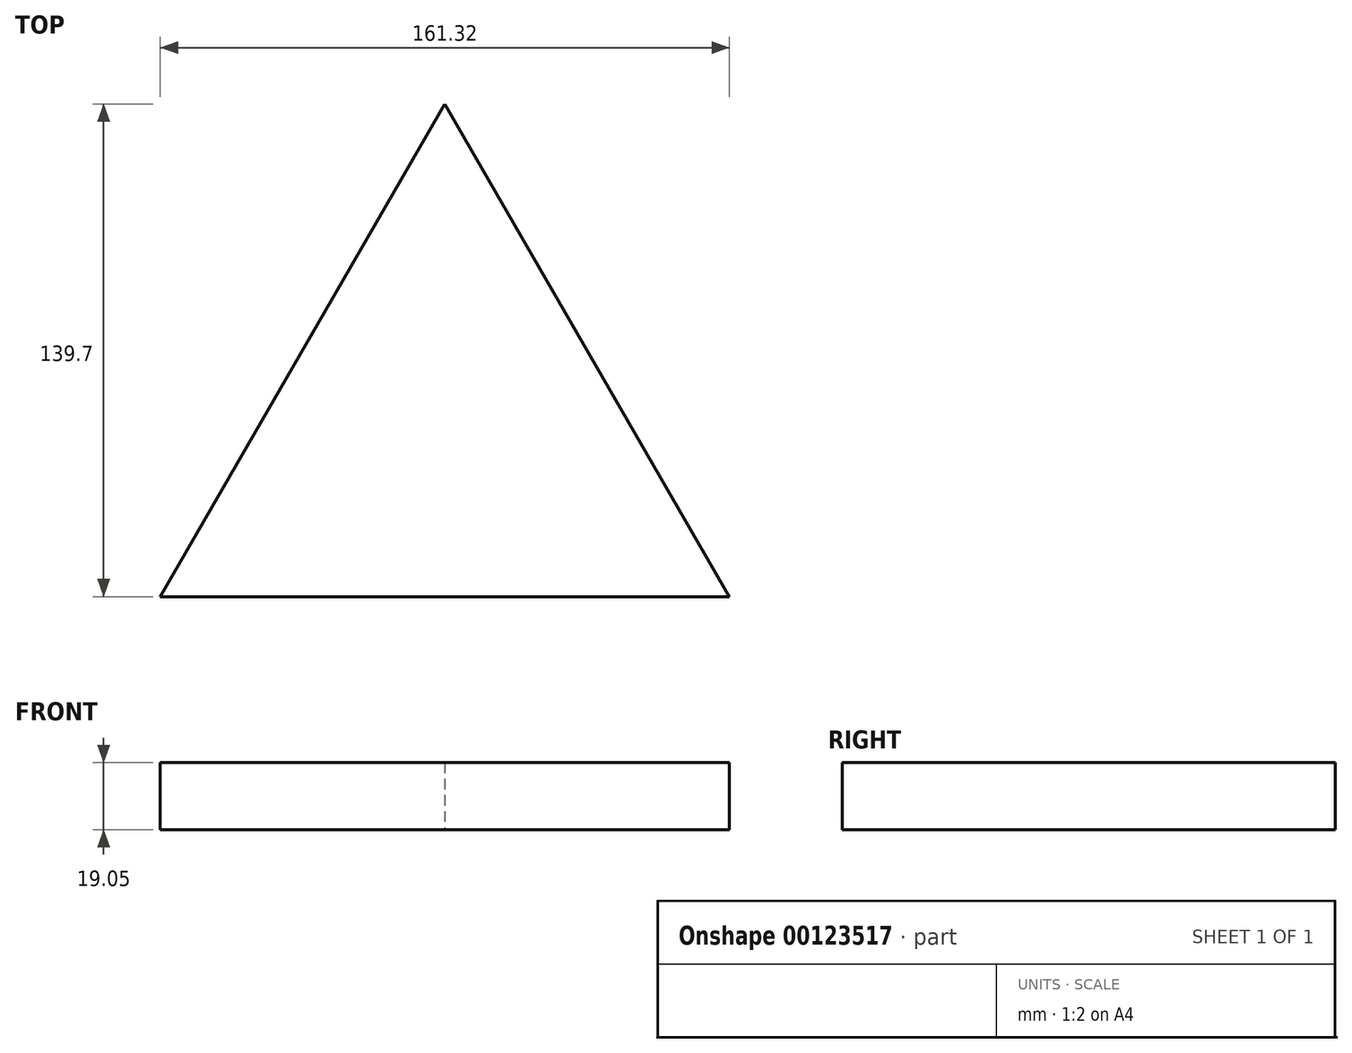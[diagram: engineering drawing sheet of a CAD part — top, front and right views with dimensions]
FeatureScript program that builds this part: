
annotation { "Feature Type Name" : "Feature", "Feature Type Description" : "" }
export const myFeature = defineFeature(function(context is Context, id is Id, definition is map)
    precondition{}
    {
        {
            var Q0;
            Q0=qCreatedBy(makeId("Top.planeOp"),FACE);
            var sketch = newSketch(context, id + "F0", { "sketchPlane" : qUnion([Q0])});
            skLineSegment(sketch, "E0", {"start": v(-80.66, -62.25) * mm, "end": v(0, 77.45) * mm});
            skLineSegment(sketch, "E1", {"start": v(80.66, -62.25) * mm, "end": v(-80.66, -62.25) * mm});
            skLineSegment(sketch, "E2", {"start": v(0, 77.45) * mm, "end": v(80.66, -62.25) * mm});
            skSolve(sketch);
        }
        {
            var Q0;
            Q0 = qSketchRegion(id + "F0", true);
            extrude(context, id + "F1", {"entities" : qUnion([Q0]), "depth" : 19.05 * mm});
        }
    });
